# Revit family: Talos RDR-S01
name_source: partatom
category: Türen
revit_build: Autodesk Revit 2016 (Build: 20150220_1215(x64)
units: mm (PartAtom-declared; Revit-internal decimal feet)

## family parameters
Beim Laden mit Abzugskörper schneiden = Nein
Gemeinsam genutzt = Nein
Immer vertikal = Ja
OmniClass-Nummer = 23.30.10.00
OmniClass-Titel = Doors
Raumberechnungspunkt = Nein

## types (7) — shared parameters
Analytische Konstruktion = <Keine Auswahl>
CoverWidth = 130 mm  [stored 0.426509 ft]
Design country = Germany
Dicke = 63 mm  [stored 0.206693 ft]
Edition number = 1
ElementWeight = 0.00 kg
FrameMaterial = 1.4401 - A4
Funktion = Außen
HandlePosition = 35 mm  [stored 0.114829 ft]
HasCover = Ja
HasGrabHandles = Ja
HasShellTopFrame = Ja
Hersteller = Kaba GmbH
Konstruktionstyp = Revolving Door
Manufacturer country = Germany
Manufacturer name = DORMA
Manufacturer_2 = Kaba GmbH
Material main = Glass
Material secondary = Metal
Modell = Talos RDR-E01
Nominal height = 2230
OperatingWeight = 0.00 kg
Product Guid = c2597803-4e53-4645-9ceb-72f15c2d1ad1
Product SKU = Talos_RDR-S01
RubberMaterial = Zellkautschuk - EPDM
SectionWidth = 4300 mm
ShutOffDevice = Nein
Technical description = http://www.kaba.com
URL = http://www.kaba.com
Weight = 0.00 kg
zero-valued in all types: Nominal width

## per-type parameters (varying)
- RDR-S01 2000: AccessLengthOrRadius=1030 mm; BaseType=>= 60 mm; ClearHeight=2100 mm; ConsoleS1=1081 mm  [stored 3.54659 ft]; ConsoleS2=1081 mm  [stored 3.54659 ft]; ConsoleType=console : Type 4; CoverMaterial=1.0980 - S420 MC; Diameter=1060 mm; DiameterCoverFront=1140 mm  [stored 3.74016 ft]; DiameterGlassInside=1040 mm  [stored 3.41207 ft]; DiameterGlassOutside=1050 mm  [stored 3.44488 ft]; DiameterNightLock=1090 mm  [stored 3.57612 ft]; DiameterNightLockCover=1120 mm; DiameterNightLockFrame=1081 mm  [stored 3.54659 ft]; DiameterNightLockGlassInside=1101 mm; DiameterNightLockGlassOutside=1109 mm  [stored 3.63845 ft]; DoorWidth=970 mm  [stored 3.18241 ft]; HandleMaterial=PA6.6 Gf30(schwarz); HasConsoleS1=Nein; HasConsoleS2=Nein; HasGrabHandles 120=Nein; HasGrabHandles 180=Ja; HasIntegralShutOffDevice=Nein; HasLock=Nein; HasLockInside=Nein; HasMotionSensor=Nein; Height=2230 mm; MotionSensorInside=1060 mm; MotionSensorOutside=1060 mm; OuterDiameter=2100 mm; RotationInterval 120=Nein; RotationInterval 180=Ja; ShutOffDeviceInside=Nein; StandardUsed=17; Type=Talos RDR-S01; Width=2100 mm
- RDR-S01 2200: AccessLengthOrRadius=1130 mm; BaseType=>= 60 mm; ClearHeight=2200 mm; ConsoleS1=1181 mm  [stored 3.87467 ft]; ConsoleS2=1181 mm  [stored 3.87467 ft]; ConsoleType=console : Type 4; CoverMaterial=Glas; Diameter=1160 mm  [stored 3.80577 ft]; DiameterCoverFront=1240 mm; DiameterGlassInside=1140 mm  [stored 3.74016 ft]; DiameterGlassOutside=1150 mm; DiameterNightLock=1190 mm  [stored 3.9042 ft]; DiameterNightLockCover=1220 mm  [stored 4.00262 ft]; DiameterNightLockFrame=1181 mm  [stored 3.87467 ft]; DiameterNightLockGlassInside=1201 mm; DiameterNightLockGlassOutside=1209 mm  [stored 3.96654 ft]; DoorWidth=1070 mm; HandleMaterial=1.4401 - A4; HasConsoleS1=Ja; HasConsoleS2=Ja; HasGrabHandles 120=Ja; HasGrabHandles 180=Nein; HasIntegralShutOffDevice=Nein; HasLock=Nein; HasLockInside=Nein; HasMotionSensor=Ja; Height=2330 mm; MotionSensorInside=1160 mm  [stored 3.80577 ft]; MotionSensorOutside=1160 mm  [stored 3.80577 ft]; MotorDriveType=K8-SA1/G4-SA3; OuterDiameter=2300 mm; RotationInterval 120=Ja; RotationInterval 180=Nein; ShutOffDeviceInside=Nein; StandardUsed=18; Type=Talos RDR-S01; Width=2300 mm
- RDR-S01 2400: AccessLengthOrRadius=1230 mm  [stored 4.03543 ft]; BaseType=>= 280 mm; ClearHeight=2300 mm; ConsoleS1=1281 mm  [stored 4.20276 ft]; ConsoleS2=1281 mm  [stored 4.20276 ft]; ConsoleType=console : Type 5; CoverMaterial=Glas; Diameter=1260 mm  [stored 4.13386 ft]; DiameterCoverFront=1340 mm  [stored 4.39633 ft]; DiameterGlassInside=1240 mm; DiameterGlassOutside=1250 mm  [stored 4.10105 ft]; DiameterNightLock=1290 mm  [stored 4.23228 ft]; DiameterNightLockCover=1320 mm  [stored 4.33071 ft]; DiameterNightLockFrame=1281 mm  [stored 4.20276 ft]; DiameterNightLockGlassInside=1301 mm; DiameterNightLockGlassOutside=1309 mm  [stored 4.29462 ft]; DoorWidth=1170 mm  [stored 3.83858 ft]; HandleMaterial=PA6.6 Gf30(schwarz); HasConsoleS1=Ja; HasConsoleS2=Ja; HasGrabHandles 120=Nein; HasGrabHandles 180=Ja; HasIntegralShutOffDevice=Nein; HasLock=Nein; HasLockInside=Nein; HasMotionSensor=Ja; Height=2430 mm; MotionSensorInside=1260 mm  [stored 4.13386 ft]; MotionSensorOutside=1260 mm  [stored 4.13386 ft]; MotorDriveType=K8-SA2; OuterDiameter=2500 mm; RotationInterval 120=Nein; RotationInterval 180=Ja; ShutOffDeviceInside=Nein; StandardUsed=19; Type=Talos RDR-S01; Width=2500 mm
- RDR-S01 2600: AccessLengthOrRadius=1330 mm  [stored 4.36352 ft]; BaseType=>= 280 mm; ClearHeight=2100 mm; ConsoleS1=1381 mm; ConsoleS2=1429 mm; ConsoleType=console : Type 5; CoverMaterial=Glas; Diameter=1360 mm  [stored 4.46194 ft]; DiameterCoverFront=1440 mm; DiameterGlassInside=1340 mm  [stored 4.39633 ft]; DiameterGlassOutside=1350 mm  [stored 4.42913 ft]; DiameterNightLock=1390 mm; DiameterNightLockCover=1420 mm; DiameterNightLockFrame=1381 mm; DiameterNightLockGlassInside=1401 mm; DiameterNightLockGlassOutside=1409 mm; DoorWidth=1270 mm; HandleMaterial=1.4401 - A4; HasConsoleS1=Nein; HasConsoleS2=Nein; HasGrabHandles 120=Ja; HasGrabHandles 180=Nein; HasIntegralShutOffDevice=Nein; HasLock=Ja; HasLockInside=Nein; HasMotionSensor=Ja; Height=2230 mm; MotionSensorInside=1360 mm  [stored 4.46194 ft]; MotionSensorOutside=1422 mm; MotorDriveType=K8-SA1/G4-SA3; OuterDiameter=2700 mm; RotationInterval 120=Ja; RotationInterval 180=Nein; ShutOffDeviceInside=Nein; StandardUsed=20; Type=Talos RDR-S01; Width=2700 mm
- RDR-S01 2800: AccessLengthOrRadius=1430 mm; BaseType=>= 280 mm; ClearHeight=2200 mm; ConsoleS1=1481 mm; ConsoleS2=1481 mm; ConsoleType=console : Type 4; CoverMaterial=Glas; Diameter=1460 mm; DiameterCoverFront=1540 mm; DiameterGlassInside=1440 mm; DiameterGlassOutside=1450 mm; DiameterNightLock=1490 mm; DiameterNightLockCover=1520 mm; DiameterNightLockFrame=1481 mm; DiameterNightLockGlassInside=1501 mm; DiameterNightLockGlassOutside=1509 mm; DoorWidth=1370 mm; HandleMaterial=PA6.6 Gf30(schwarz); HasConsoleS1=Ja; HasConsoleS2=Ja; HasGrabHandles 120=Nein; HasGrabHandles 180=Ja; HasIntegralShutOffDevice=Nein; HasLock=Nein; HasLockInside=Nein; HasMotionSensor=Ja; Height=2330 mm; MotionSensorInside=1460 mm; MotionSensorOutside=1460 mm; MotorDriveType=K8-SA1/G4-SA3; OuterDiameter=2900 mm; RotationInterval 120=Nein; RotationInterval 180=Ja; ShutOffDeviceInside=Nein; StandardUsed=21; Type=Talos RDR-S01; Width=2900 mm
- RDR-S01 3000: AccessLengthOrRadius=1530 mm; BaseType=>= 280 mm; ClearHeight=2300 mm; ConsoleS1=1581 mm; ConsoleS2=1629 mm; ConsoleType=console : Type 5; CoverMaterial=1.0980 - S420 MC; Diameter=1560 mm; DiameterCoverFront=1640 mm; DiameterGlassInside=1540 mm; DiameterGlassOutside=1550 mm; DiameterNightLock=1590 mm; DiameterNightLockCover=1620 mm; DiameterNightLockFrame=1581 mm; DiameterNightLockGlassInside=1601 mm; DiameterNightLockGlassOutside=1609 mm; DoorWidth=1470 mm; HandleMaterial=1.4401 - A4; HasConsoleS1=Ja; HasConsoleS2=Ja; HasGrabHandles 120=Ja; HasGrabHandles 180=Nein; HasIntegralShutOffDevice=Ja; HasLock=Ja; HasLockInside=Nein; HasMotionSensor=Nein; Height=2430 mm; MotionSensorInside=1560 mm; MotionSensorOutside=1622 mm; MotorDriveType=K8-SA1; OuterDiameter=3100 mm; RotationInterval 120=Ja; RotationInterval 180=Nein; ShutOffDeviceInside=Ja; StandardUsed=22; Type=Talos RDR-E01; Width=3100 mm
- RDR-S01 2000h: AccessLengthOrRadius=1030 mm; BaseType=>= 60 mm; ClearHeight=2800 mm; ConsoleS1=1129 mm; ConsoleS2=1081 mm  [stored 3.54659 ft]; ConsoleType=console : Type 4; CoverMaterial=Glas; Diameter=1060 mm; DiameterCoverFront=1140 mm  [stored 3.74016 ft]; DiameterGlassInside=1040 mm  [stored 3.41207 ft]; DiameterGlassOutside=1050 mm  [stored 3.44488 ft]; DiameterNightLock=1090 mm  [stored 3.57612 ft]; DiameterNightLockCover=1120 mm; DiameterNightLockFrame=1081 mm  [stored 3.54659 ft]; DiameterNightLockGlassInside=1101 mm; DiameterNightLockGlassOutside=1109 mm  [stored 3.63845 ft]; DoorWidth=970 mm  [stored 3.18241 ft]; HandleMaterial=PA6.6 Gf30(schwarz); HasConsoleS1=Nein; HasConsoleS2=Nein; HasGrabHandles 120=Nein; HasGrabHandles 180=Ja; HasIntegralShutOffDevice=Nein; HasLock=Nein; HasLockInside=Ja; HasMotionSensor=Ja; Height=2930 mm; MotionSensorInside=1122 mm  [stored 3.6811 ft]; MotionSensorOutside=1060 mm; MotorDriveType=-; OuterDiameter=2100 mm; RotationInterval 120=Nein; RotationInterval 180=Ja; ShutOffDeviceInside=Nein; StandardUsed=23; Type=Talos RDR-S01; Width=2100 mm

note: [stored X ft] marks values corroborated as IEEE doubles in the binary element streams (Revit-internal decimal feet)
